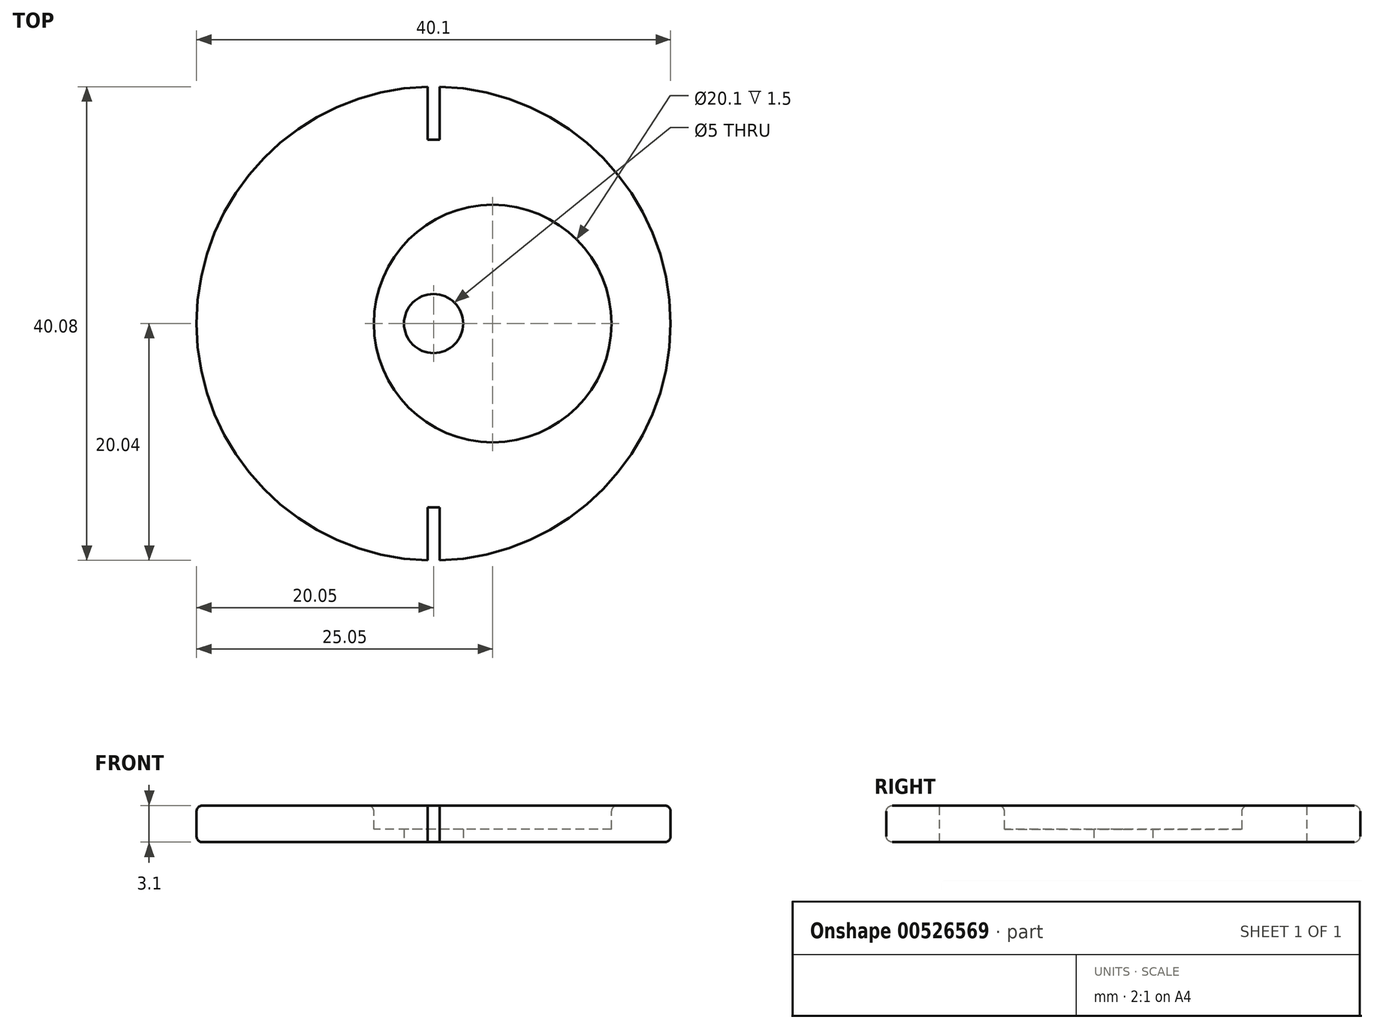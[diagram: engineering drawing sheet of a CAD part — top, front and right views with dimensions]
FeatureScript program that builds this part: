
annotation { "Feature Type Name" : "Feature", "Feature Type Description" : "" }
export const myFeature = defineFeature(function(context is Context, id is Id, definition is map)
    precondition{}
    {
        {
            var Q0;
            Q0=qCreatedBy(makeId("Top.planeOp"),FACE);
            var sketch = newSketch(context, id + "F0", { "sketchPlane" : qUnion([Q0])});
            skCircle(sketch, "E0", {"center": v(0, 0) * mm, "radius": 20.05 * mm});
            skSolve(sketch);
        }
        {
            var Q0;
            Q0=qSketchRegion(id+"F0",true);
            extrude(context, id + "F1", {"entities" : qUnion([Q0]), "depth" : 3.1 * mm});
        }
        {
            var Q0;
            Q0=makeQuery(id+"F1.opExtrude","CAP_FACE",FACE,{"disambiguationData":[OSD([sQuery(id+"F0.wireOp",EDGE,"E0")])],"isStart":false});
            var sketch = newSketch(context, id + "F2", { "sketchPlane" : qUnion([Q0])});
            skCircle(sketch, "E1", {"center": v(5, 0) * mm, "radius": 10.05 * mm});
            skSolve(sketch);
        }
        {
            var Q0;
            Q0=qSketchRegion(id+"F2",true);
            extrude(context, id + "F3", {"entities" : qUnion([Q0]), "operationType" : NewBodyOperationType.REMOVE, "oppositeDirection" : true, "depth" : 2 * mm});
        }
        {
            var Q0;
            Q0=makeQuery(id+"F1.opExtrude","CAP_FACE",FACE,{"disambiguationData":[OSD([sQuery(id+"F0.wireOp",EDGE,"E0")])],"isStart":false});
            var Q1;
            Q1=makeQuery(id+"F1.opExtrude","CAP_FACE",FACE,{"disambiguationData":[OSD([sQuery(id+"F0.wireOp",EDGE,"E0")])],"isStart":true});
            fillet(context, id + "F4", {"entities" : qUnion([Q0, Q1]), "radius" : 0.5 * mm, "tangentPropagation" : true, "allowEdgeOverflow" : false});
        }
        {
            var Q0;
            Q0=makeQuery(id+"F1.opExtrude","CAP_FACE",FACE,{"disambiguationData":[OSD([sQuery(id+"F0.wireOp",EDGE,"E0")])],"isStart":true});
            var sketch = newSketch(context, id + "F5", { "sketchPlane" : qUnion([Q0])});
            skCircle(sketch, "E2", {"center": v(0, 0) * mm, "radius": 2.5 * mm});
            skSolve(sketch);
        }
        {
            var Q0;
            Q0=qSketchRegion(id+"F5",true);
            extrude(context, id + "F6", {"entities" : qUnion([Q0]), "operationType" : NewBodyOperationType.REMOVE, "endBound" : BoundingType.THROUGH_ALL, "oppositeDirection" : true, "depth" : 25 * mm});
        }
        {
            var Q0;
            Q0=makeQuery(id+"F1.opExtrude","CAP_FACE",FACE,{"disambiguationData":[OSD([sQuery(id+"F0.wireOp",EDGE,"E0")])],"isStart":false});
            var sketch = newSketch(context, id + "F7", { "sketchPlane" : qUnion([Q0])});
            skLineSegment(sketch, "E3.bottom", {"start": v(-0.5, 20.55) * mm, "end": v(0.5, 20.55) * mm});
            skLineSegment(sketch, "E3.top", {"start": v(-0.5, 15.55) * mm, "end": v(0.5, 15.55) * mm});
            skLineSegment(sketch, "E3.left", {"start": v(-0.5, 20.55) * mm, "end": v(-0.5, 15.55) * mm});
            skLineSegment(sketch, "E3.right", {"start": v(0.5, 20.55) * mm, "end": v(0.5, 15.55) * mm});
            skPoint(sketch, "E3.middle", {"position": v(0, 18.05) * mm});
            skLineSegment(sketch, "E4.MirrorCS", {"start": v(-0.5, -15.55) * mm, "end": v(0.5, -15.55) * mm});
            skLineSegment(sketch, "E5.MirrorCS", {"start": v(-0.5, -20.55) * mm, "end": v(0.5, -20.55) * mm});
            skLineSegment(sketch, "E6.MirrorCS", {"start": v(-0.5, -20.55) * mm, "end": v(-0.5, -15.55) * mm});
            skPoint(sketch, "E7.MirrorP", {"position": v(0, -18.05) * mm});
            skLineSegment(sketch, "E8.MirrorCS", {"start": v(0.5, -20.55) * mm, "end": v(0.5, -15.55) * mm});
            skSolve(sketch);
        }
        {
            var Q0;
            Q0 = qSketchRegion(id + "F7", true);
            extrude(context, id + "F8", {"entities" : qUnion([Q0]), "operationType" : NewBodyOperationType.REMOVE, "endBound" : BoundingType.THROUGH_ALL, "oppositeDirection" : true, "depth" : 25 * mm, "offsetDistance" : 25 * mm});
        }
    });
